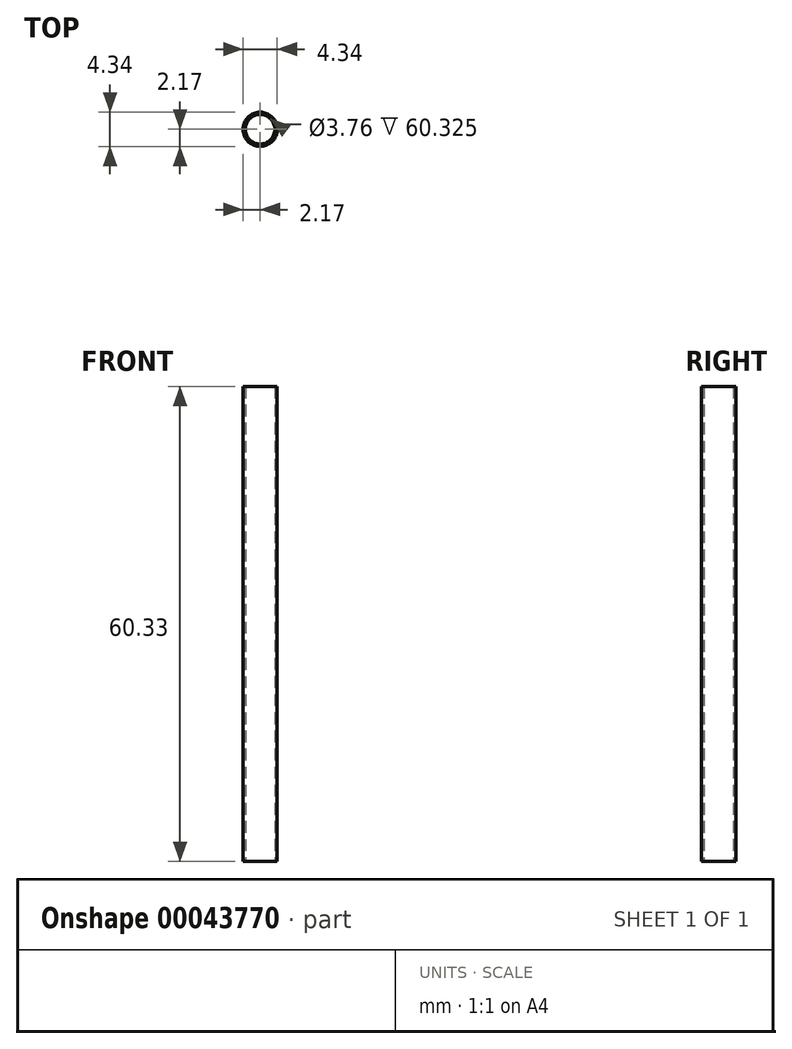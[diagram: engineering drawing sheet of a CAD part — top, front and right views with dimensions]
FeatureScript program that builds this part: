
annotation { "Feature Type Name" : "Feature", "Feature Type Description" : "" }
export const myFeature = defineFeature(function(context is Context, id is Id, definition is map)
    precondition{}
    {
        {
            var Q0;
            Q0=qCreatedBy(makeId("Front.planeOp"),FACE);
            var sketch = newSketch(context, id + "F0", { "sketchPlane" : qUnion([Q0])});
            skLineSegment(sketch, "E0", {"start": v(0, 0) * mm, "end": v(1.88, 0) * mm});
            skLineSegment(sketch, "E1", {"start": v(1.88, 0) * mm, "end": v(1.88, 60.33) * mm});
            skLineSegment(sketch, "E2", {"start": v(1.88, 60.33) * mm, "end": v(2.17, 60.33) * mm});
            skLineSegment(sketch, "E3", {"start": v(2.17, 60.33) * mm, "end": v(2.17, 0) * mm});
            skLineSegment(sketch, "E4", {"start": v(2.17, 0) * mm, "end": v(1.88, 0) * mm});
            skLineSegment(sketch, "E5", {"start": v(0, 0) * mm, "end": v(0, 60.33) * mm});
            skLineSegment(sketch, "E6", {"start": v(0, 60.33) * mm, "end": v(1.88, 60.33) * mm});
            skSolve(sketch);
        }
        {
            var Q0;
            Q0=makeQuery(id+"F0.imprint","IMPRINT",FACE,{"disambiguationData":[TD([[makeQuery(id+"F0.imprint","IMPRINT",EDGE,{"derivedFrom":sQuery(id+"F0.wireOp",EDGE,"E1")}),-1.0]])]});
            var Q1;
            Q1=sQuery(id+"F0.wireOp",EDGE,"E5");
            revolve(context, id + "F1", {"entities" : qUnion([Q0]), "axis" : qUnion([Q1]), "revolveType" : RevolveType.FULL});
        }
    });
